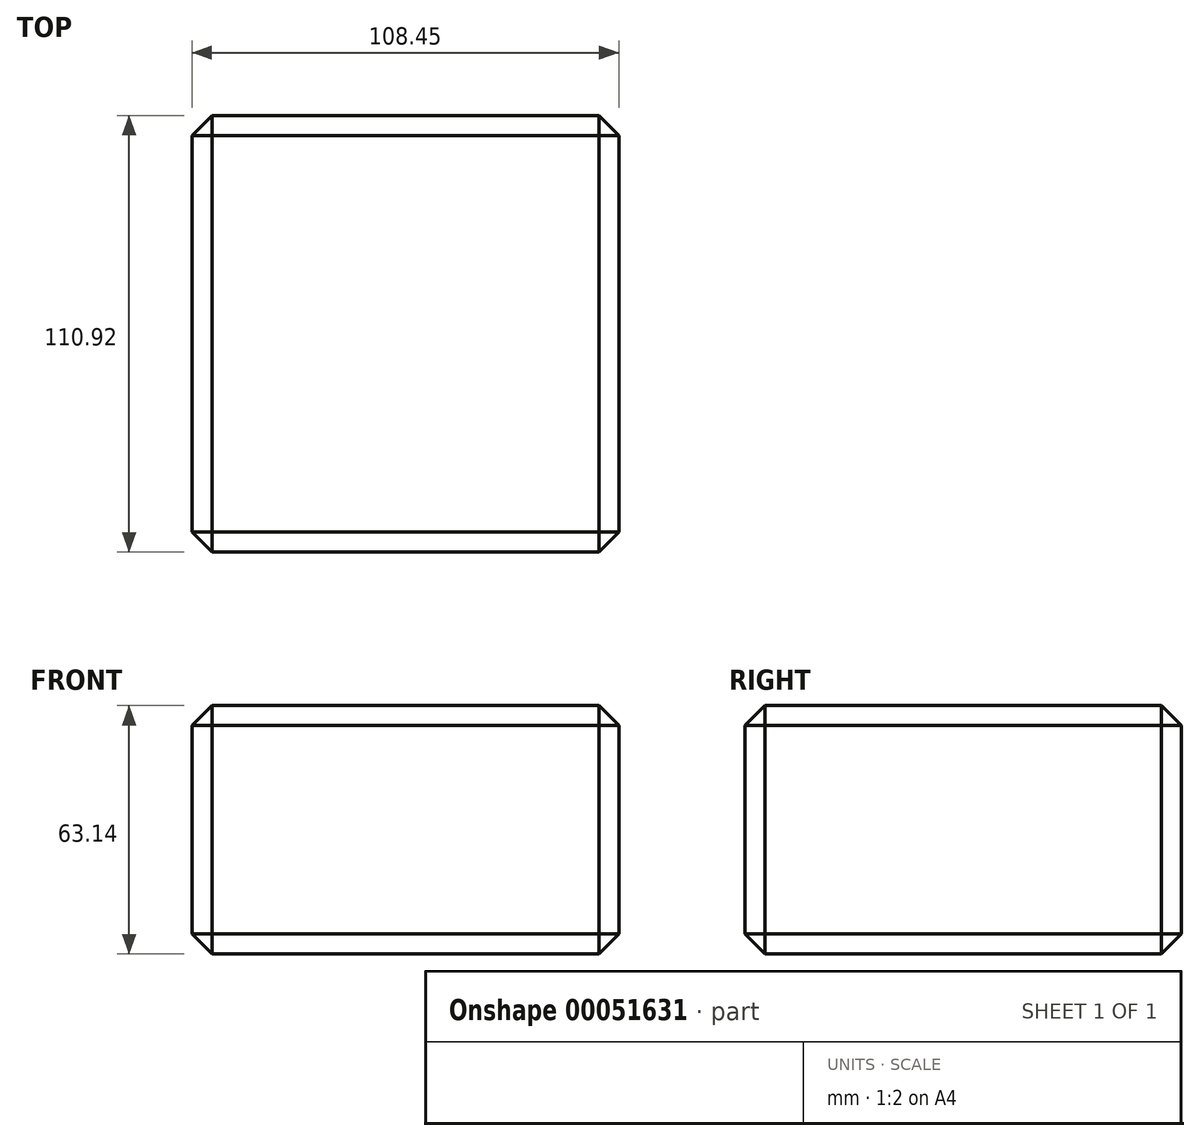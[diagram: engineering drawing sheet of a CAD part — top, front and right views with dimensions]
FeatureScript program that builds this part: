
annotation { "Feature Type Name" : "Feature", "Feature Type Description" : "" }
export const myFeature = defineFeature(function(context is Context, id is Id, definition is map)
    precondition{}
    {
        {
            var Q0;
            Q0=qCreatedBy(makeId("Front.planeOp"),FACE);
            var sketch = newSketch(context, id + "F0", { "sketchPlane" : qUnion([Q0])});
            skLineSegment(sketch, "E0.bottom", {"start": v(-59.19, 27.6) * mm, "end": v(49.26, 27.6) * mm});
            skLineSegment(sketch, "E0.top", {"start": v(-59.19, -35.54) * mm, "end": v(49.26, -35.54) * mm});
            skLineSegment(sketch, "E0.left", {"start": v(-59.19, 27.6) * mm, "end": v(-59.19, -35.54) * mm});
            skLineSegment(sketch, "E0.right", {"start": v(49.26, 27.6) * mm, "end": v(49.26, -35.54) * mm});
            skSolve(sketch);
        }
        {
            var Q0;
            Q0=makeQuery(id+"F0.imprint","IMPRINT",FACE,{"disambiguationData":[TD([[makeQuery(id+"F0.imprint","IMPRINT",EDGE,{"derivedFrom":sQuery(id+"F0.wireOp",EDGE,"E0.bottom")}),-1.0]])]});
            extrude(context, id + "F1", {"entities" : qUnion([Q0]), "depth" : 110.92 * mm});
        }
        {
            var Q0;
            Q0=makeQuery(id+"F1.opExtrude","SWEPT_EDGE",EDGE,{"disambiguationData":[OSD([sQuery(id+"F0.wireOp",EDGE,"E0.bottom"),sQuery(id+"F0.wireOp",EDGE,"E0.right")])]});
            var Q1;
            Q1=makeQuery(id+"F1.opExtrude","CAP_EDGE",EDGE,{"disambiguationData":[OSD([sQuery(id+"F0.wireOp",EDGE,"E0.bottom")])],"isStart":false});
            var Q2;
            Q2=makeQuery(id+"F1.opExtrude","CAP_EDGE",EDGE,{"disambiguationData":[OSD([sQuery(id+"F0.wireOp",EDGE,"E0.right")])],"isStart":false});
            var Q3;
            Q3=makeQuery(id+"F1.opExtrude","CAP_FACE",FACE,{"disambiguationData":[OSD([sQuery(id+"F0.wireOp",EDGE,"E0.bottom"),sQuery(id+"F0.wireOp",EDGE,"E0.top"),sQuery(id+"F0.wireOp",EDGE,"E0.left"),sQuery(id+"F0.wireOp",EDGE,"E0.right")])],"isStart":false});
            var Q4;
            Q4=makeQuery(id+"F1.opExtrude","SWEPT_EDGE",EDGE,{"disambiguationData":[OSD([sQuery(id+"F0.wireOp",EDGE,"E0.top"),sQuery(id+"F0.wireOp",EDGE,"E0.right")])]});
            var Q5;
            Q5=makeQuery(id+"F1.opExtrude","SWEPT_EDGE",EDGE,{"disambiguationData":[OSD([sQuery(id+"F0.wireOp",EDGE,"E0.bottom"),sQuery(id+"F0.wireOp",EDGE,"E0.left")])]});
            var Q6;
            Q6=makeQuery(id+"F1.opExtrude","SWEPT_EDGE",EDGE,{"disambiguationData":[OSD([sQuery(id+"F0.wireOp",EDGE,"E0.top"),sQuery(id+"F0.wireOp",EDGE,"E0.left")])]});
            var Q7;
            Q7=makeQuery(id+"F1.opExtrude","CAP_EDGE",EDGE,{"disambiguationData":[OSD([sQuery(id+"F0.wireOp",EDGE,"E0.top")])],"isStart":true});
            var Q8;
            Q8=makeQuery(id+"F1.opExtrude","CAP_EDGE",EDGE,{"disambiguationData":[OSD([sQuery(id+"F0.wireOp",EDGE,"E0.left")])],"isStart":true});
            var Q9;
            Q9=makeQuery(id+"F1.opExtrude","SWEPT_FACE",FACE,{"disambiguationData":[OSD([sQuery(id+"F0.wireOp",EDGE,"E0.bottom")])]});
            var Q10;
            Q10=makeQuery(id+"F1.opExtrude","CAP_FACE",FACE,{"disambiguationData":[OSD([sQuery(id+"F0.wireOp",EDGE,"E0.bottom"),sQuery(id+"F0.wireOp",EDGE,"E0.top"),sQuery(id+"F0.wireOp",EDGE,"E0.left"),sQuery(id+"F0.wireOp",EDGE,"E0.right")])],"isStart":true});
            chamfer(context, id + "F2", {"entities" : qUnion([Q0, Q1, Q2, Q3, Q4, Q5, Q6, Q7, Q8, Q9, Q10]), "width" : 5.08 * mm, "tangentPropagation" : true});
        }
    });
